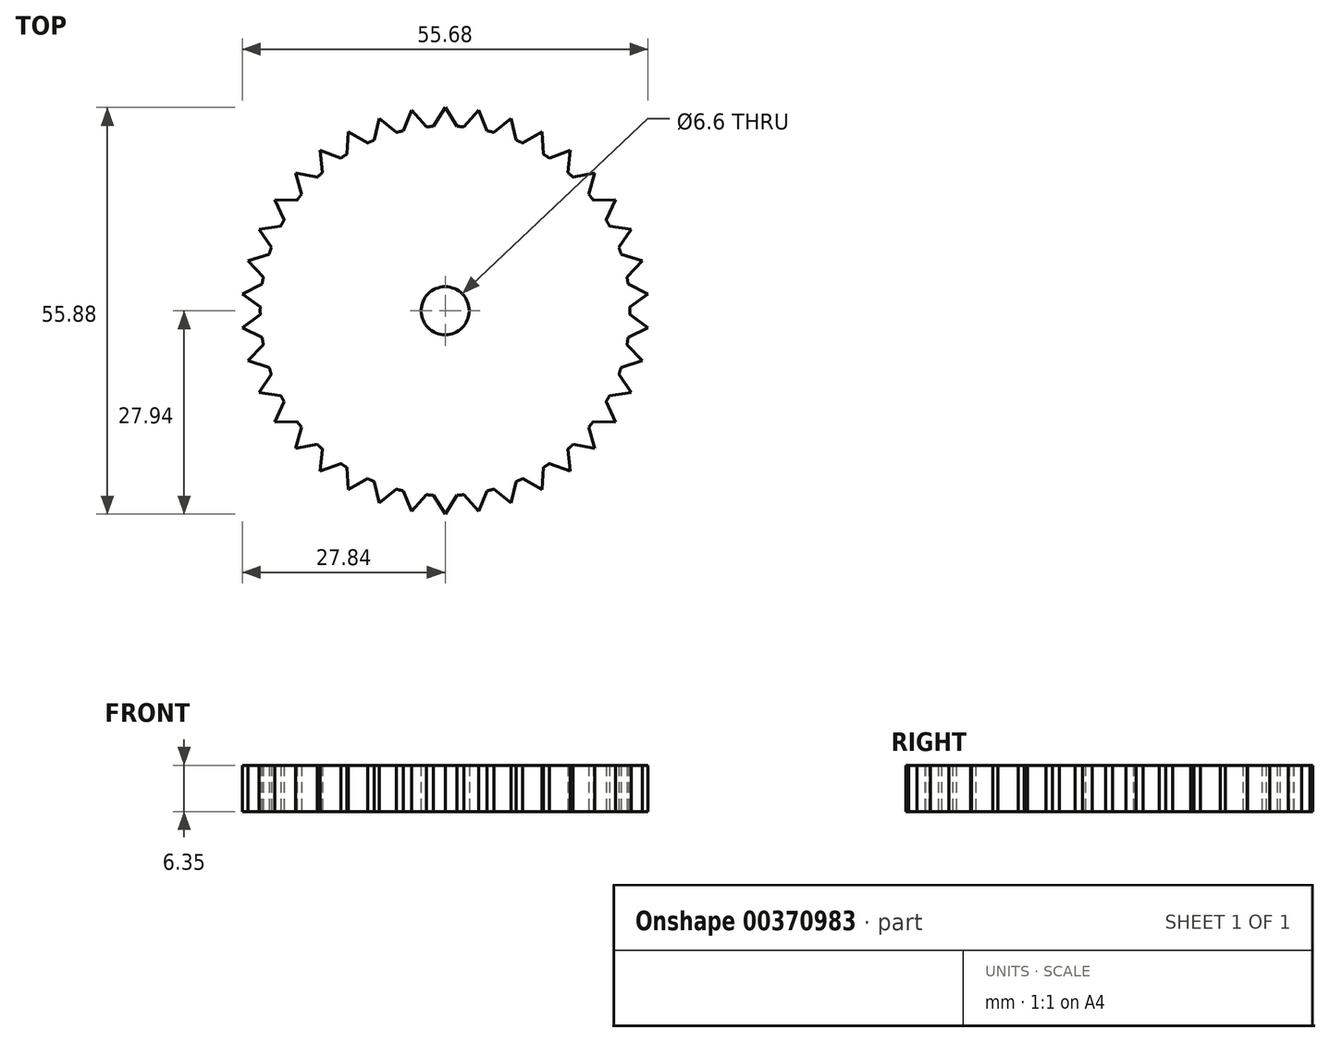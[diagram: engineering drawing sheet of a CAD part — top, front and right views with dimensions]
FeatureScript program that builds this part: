
annotation { "Feature Type Name" : "Feature", "Feature Type Description" : "" }
export const myFeature = defineFeature(function(context is Context, id is Id, definition is map)
    precondition{}
    {
        {
            var Q0;
            Q0=qCreatedBy(makeId("Top.planeOp"),FACE);
            var sketch = newSketch(context, id + "F0", { "sketchPlane" : qUnion([Q0])});
            skCircle(sketch, "E0", {"center": v(0, 0) * mm, "radius": 25.4 * mm});
            skCircle(sketch, "E1", {"center": v(0, 0) * mm, "radius": 3.3 * mm});
            skLineSegment(sketch, "E2", {"start": v(0, 25.4) * mm, "end": v(0, 27.94) * mm});
            skLineSegment(sketch, "E3", {"start": v(0, 27.94) * mm, "end": v(1.6, 25.35) * mm});
            skLineSegment(sketch, "E4", {"start": v(1.6, 25.35) * mm, "end": v(0, 27.94) * mm});
            skLineSegment(sketch, "E5", {"start": v(0, 27.94) * mm, "end": v(-1.6, 25.35) * mm});
            skLineSegment(sketch, "E6.1.0", {"start": v(-2.59, 25.27) * mm, "end": v(-4.6, 27.56) * mm});
            skLineSegment(sketch, "E6.1.1", {"start": v(-4.6, 27.56) * mm, "end": v(-5.76, 24.74) * mm});
            skLineSegment(sketch, "E6.2.0", {"start": v(-6.71, 24.5) * mm, "end": v(-9.07, 26.43) * mm});
            skLineSegment(sketch, "E6.2.1", {"start": v(-9.07, 26.43) * mm, "end": v(-9.75, 23.45) * mm});
            skLineSegment(sketch, "E6.3.0", {"start": v(-10.65, 23.06) * mm, "end": v(-13.3, 24.57) * mm});
            skLineSegment(sketch, "E6.3.1", {"start": v(-13.3, 24.57) * mm, "end": v(-13.48, 21.53) * mm});
            skLineSegment(sketch, "E6.4.0", {"start": v(-14.3, 21) * mm, "end": v(-17.16, 22.05) * mm});
            skLineSegment(sketch, "E6.4.1", {"start": v(-17.16, 22.05) * mm, "end": v(-16.84, 19.02) * mm});
            skLineSegment(sketch, "E6.5.0", {"start": v(-17.56, 18.35) * mm, "end": v(-20.56, 18.92) * mm});
            skLineSegment(sketch, "E6.5.1", {"start": v(-20.56, 18.92) * mm, "end": v(-19.74, 15.99) * mm});
            skLineSegment(sketch, "E6.6.0", {"start": v(-20.34, 15.2) * mm, "end": v(-23.4, 15.28) * mm});
            skLineSegment(sketch, "E6.6.1", {"start": v(-23.4, 15.28) * mm, "end": v(-22.1, 12.52) * mm});
            skLineSegment(sketch, "E6.7.0", {"start": v(-22.57, 11.65) * mm, "end": v(-25.59, 11.22) * mm});
            skLineSegment(sketch, "E6.7.1", {"start": v(-25.59, 11.22) * mm, "end": v(-23.86, 8.71) * mm});
            skLineSegment(sketch, "E6.8.0", {"start": v(-24.18, 7.78) * mm, "end": v(-27.09, 6.86) * mm});
            skLineSegment(sketch, "E6.8.1", {"start": v(-27.09, 6.86) * mm, "end": v(-24.97, 4.67) * mm});
            skLineSegment(sketch, "E6.9.0", {"start": v(-25.13, 3.7) * mm, "end": v(-27.84, 2.3) * mm});
            skLineSegment(sketch, "E6.9.1", {"start": v(-27.84, 2.3) * mm, "end": v(-25.4, 0.5) * mm});
            skLineSegment(sketch, "E6.10.0", {"start": v(-25.4, -0.5) * mm, "end": v(-27.84, -2.3) * mm});
            skLineSegment(sketch, "E6.10.1", {"start": v(-27.84, -2.3) * mm, "end": v(-25.13, -3.7) * mm});
            skLineSegment(sketch, "E6.11.0", {"start": v(-24.97, -4.67) * mm, "end": v(-27.09, -6.86) * mm});
            skLineSegment(sketch, "E6.11.1", {"start": v(-27.09, -6.86) * mm, "end": v(-24.18, -7.78) * mm});
            skLineSegment(sketch, "E6.12.0", {"start": v(-23.86, -8.71) * mm, "end": v(-25.59, -11.22) * mm});
            skLineSegment(sketch, "E6.12.1", {"start": v(-25.59, -11.22) * mm, "end": v(-22.57, -11.65) * mm});
            skLineSegment(sketch, "E6.13.0", {"start": v(-22.1, -12.52) * mm, "end": v(-23.4, -15.28) * mm});
            skLineSegment(sketch, "E6.13.1", {"start": v(-23.4, -15.28) * mm, "end": v(-20.34, -15.2) * mm});
            skLineSegment(sketch, "E6.14.0", {"start": v(-19.74, -15.99) * mm, "end": v(-20.56, -18.92) * mm});
            skLineSegment(sketch, "E6.14.1", {"start": v(-20.56, -18.92) * mm, "end": v(-17.56, -18.35) * mm});
            skLineSegment(sketch, "E6.15.0", {"start": v(-16.84, -19.02) * mm, "end": v(-17.16, -22.05) * mm});
            skLineSegment(sketch, "E6.15.1", {"start": v(-17.16, -22.05) * mm, "end": v(-14.3, -21) * mm});
            skLineSegment(sketch, "E6.16.0", {"start": v(-13.48, -21.53) * mm, "end": v(-13.3, -24.57) * mm});
            skLineSegment(sketch, "E6.16.1", {"start": v(-13.3, -24.57) * mm, "end": v(-10.65, -23.06) * mm});
            skLineSegment(sketch, "E6.17.0", {"start": v(-9.75, -23.45) * mm, "end": v(-9.07, -26.43) * mm});
            skLineSegment(sketch, "E6.17.1", {"start": v(-9.07, -26.43) * mm, "end": v(-6.71, -24.5) * mm});
            skLineSegment(sketch, "E6.18.0", {"start": v(-5.76, -24.74) * mm, "end": v(-4.6, -27.56) * mm});
            skLineSegment(sketch, "E6.18.1", {"start": v(-4.6, -27.56) * mm, "end": v(-2.59, -25.27) * mm});
            skLineSegment(sketch, "E6.19.0", {"start": v(-1.6, -25.35) * mm, "end": v(0, -27.94) * mm});
            skLineSegment(sketch, "E6.19.1", {"start": v(0, -27.94) * mm, "end": v(1.6, -25.35) * mm});
            skLineSegment(sketch, "E6.20.0", {"start": v(2.59, -25.27) * mm, "end": v(4.6, -27.56) * mm});
            skLineSegment(sketch, "E6.20.1", {"start": v(4.6, -27.56) * mm, "end": v(5.76, -24.74) * mm});
            skLineSegment(sketch, "E6.21.0", {"start": v(6.71, -24.5) * mm, "end": v(9.07, -26.43) * mm});
            skLineSegment(sketch, "E6.21.1", {"start": v(9.07, -26.43) * mm, "end": v(9.75, -23.45) * mm});
            skLineSegment(sketch, "E6.22.0", {"start": v(10.65, -23.06) * mm, "end": v(13.3, -24.57) * mm});
            skLineSegment(sketch, "E6.22.1", {"start": v(13.3, -24.57) * mm, "end": v(13.48, -21.53) * mm});
            skLineSegment(sketch, "E6.23.0", {"start": v(14.3, -21) * mm, "end": v(17.16, -22.05) * mm});
            skLineSegment(sketch, "E6.23.1", {"start": v(17.16, -22.05) * mm, "end": v(16.84, -19.02) * mm});
            skLineSegment(sketch, "E6.24.0", {"start": v(17.56, -18.35) * mm, "end": v(20.56, -18.92) * mm});
            skLineSegment(sketch, "E6.24.1", {"start": v(20.56, -18.92) * mm, "end": v(19.74, -15.99) * mm});
            skLineSegment(sketch, "E6.25.0", {"start": v(20.34, -15.2) * mm, "end": v(23.4, -15.28) * mm});
            skLineSegment(sketch, "E6.25.1", {"start": v(23.4, -15.28) * mm, "end": v(22.1, -12.52) * mm});
            skLineSegment(sketch, "E6.26.0", {"start": v(22.57, -11.65) * mm, "end": v(25.59, -11.22) * mm});
            skLineSegment(sketch, "E6.26.1", {"start": v(25.59, -11.22) * mm, "end": v(23.86, -8.71) * mm});
            skLineSegment(sketch, "E6.27.0", {"start": v(24.18, -7.78) * mm, "end": v(27.09, -6.86) * mm});
            skLineSegment(sketch, "E6.27.1", {"start": v(27.09, -6.86) * mm, "end": v(24.97, -4.67) * mm});
            skLineSegment(sketch, "E6.28.0", {"start": v(25.13, -3.7) * mm, "end": v(27.84, -2.3) * mm});
            skLineSegment(sketch, "E6.28.1", {"start": v(27.84, -2.3) * mm, "end": v(25.4, -0.5) * mm});
            skLineSegment(sketch, "E6.29.0", {"start": v(25.4, 0.5) * mm, "end": v(27.84, 2.3) * mm});
            skLineSegment(sketch, "E6.29.1", {"start": v(27.84, 2.3) * mm, "end": v(25.13, 3.7) * mm});
            skLineSegment(sketch, "E6.30.0", {"start": v(24.97, 4.67) * mm, "end": v(27.09, 6.86) * mm});
            skLineSegment(sketch, "E6.30.1", {"start": v(27.09, 6.86) * mm, "end": v(24.18, 7.78) * mm});
            skLineSegment(sketch, "E6.31.0", {"start": v(23.86, 8.71) * mm, "end": v(25.59, 11.22) * mm});
            skLineSegment(sketch, "E6.31.1", {"start": v(25.59, 11.22) * mm, "end": v(22.57, 11.65) * mm});
            skLineSegment(sketch, "E6.32.0", {"start": v(22.1, 12.52) * mm, "end": v(23.4, 15.28) * mm});
            skLineSegment(sketch, "E6.32.1", {"start": v(23.4, 15.28) * mm, "end": v(20.34, 15.2) * mm});
            skLineSegment(sketch, "E6.33.0", {"start": v(19.74, 15.99) * mm, "end": v(20.56, 18.92) * mm});
            skLineSegment(sketch, "E6.33.1", {"start": v(20.56, 18.92) * mm, "end": v(17.56, 18.35) * mm});
            skLineSegment(sketch, "E6.34.0", {"start": v(16.84, 19.02) * mm, "end": v(17.16, 22.05) * mm});
            skLineSegment(sketch, "E6.34.1", {"start": v(17.16, 22.05) * mm, "end": v(14.3, 21) * mm});
            skLineSegment(sketch, "E6.35.0", {"start": v(13.48, 21.53) * mm, "end": v(13.3, 24.57) * mm});
            skLineSegment(sketch, "E6.35.1", {"start": v(13.3, 24.57) * mm, "end": v(10.65, 23.06) * mm});
            skLineSegment(sketch, "E6.36.0", {"start": v(9.75, 23.45) * mm, "end": v(9.07, 26.43) * mm});
            skLineSegment(sketch, "E6.36.1", {"start": v(9.07, 26.43) * mm, "end": v(6.71, 24.5) * mm});
            skLineSegment(sketch, "E6.37.0", {"start": v(5.76, 24.74) * mm, "end": v(4.6, 27.56) * mm});
            skLineSegment(sketch, "E6.37.1", {"start": v(4.6, 27.56) * mm, "end": v(2.59, 25.27) * mm});
            skSolve(sketch);
        }
        {
            var Q0;
            {var subQ0=sQuery(id+"F0.wireOp",EDGE,"E6.37.0");Q0=makeQuery(id+"F0.imprint","IMPRINT",FACE,{"disambiguationData":[TD([[makeQuery(id+"F0.imprint","IMPRINT",EDGE,{"derivedFrom":subQ0}),1.0]])]});}
            var Q1;
            {var subQ0=sQuery(id+"F0.wireOp",EDGE,"E6.36.0");Q1=makeQuery(id+"F0.imprint","IMPRINT",FACE,{"disambiguationData":[TD([[makeQuery(id+"F0.imprint","IMPRINT",EDGE,{"derivedFrom":subQ0}),1.0]])]});}
            var Q2;
            {var subQ0=sQuery(id+"F0.wireOp",EDGE,"E6.35.0");Q2=makeQuery(id+"F0.imprint","IMPRINT",FACE,{"disambiguationData":[TD([[makeQuery(id+"F0.imprint","IMPRINT",EDGE,{"derivedFrom":subQ0}),1.0]])]});}
            var Q3;
            {var subQ0=sQuery(id+"F0.wireOp",EDGE,"E6.34.0");Q3=makeQuery(id+"F0.imprint","IMPRINT",FACE,{"disambiguationData":[TD([[makeQuery(id+"F0.imprint","IMPRINT",EDGE,{"derivedFrom":subQ0}),1.0]])]});}
            var Q4;
            {var subQ0=sQuery(id+"F0.wireOp",EDGE,"E6.33.0");Q4=makeQuery(id+"F0.imprint","IMPRINT",FACE,{"disambiguationData":[TD([[makeQuery(id+"F0.imprint","IMPRINT",EDGE,{"derivedFrom":subQ0}),1.0]])]});}
            var Q5;
            {var subQ0=sQuery(id+"F0.wireOp",EDGE,"E6.32.0");Q5=makeQuery(id+"F0.imprint","IMPRINT",FACE,{"disambiguationData":[TD([[makeQuery(id+"F0.imprint","IMPRINT",EDGE,{"derivedFrom":subQ0}),1.0]])]});}
            var Q6;
            {var subQ0=sQuery(id+"F0.wireOp",EDGE,"E6.31.0");Q6=makeQuery(id+"F0.imprint","IMPRINT",FACE,{"disambiguationData":[TD([[makeQuery(id+"F0.imprint","IMPRINT",EDGE,{"derivedFrom":subQ0}),1.0]])]});}
            var Q7;
            {var subQ0=sQuery(id+"F0.wireOp",EDGE,"E6.30.0");Q7=makeQuery(id+"F0.imprint","IMPRINT",FACE,{"disambiguationData":[TD([[makeQuery(id+"F0.imprint","IMPRINT",EDGE,{"derivedFrom":subQ0}),1.0]])]});}
            var Q8;
            {var subQ0=sQuery(id+"F0.wireOp",EDGE,"E6.29.0");Q8=makeQuery(id+"F0.imprint","IMPRINT",FACE,{"disambiguationData":[TD([[makeQuery(id+"F0.imprint","IMPRINT",EDGE,{"derivedFrom":subQ0}),1.0]])]});}
            var Q9;
            {var subQ0=sQuery(id+"F0.wireOp",EDGE,"E6.28.0");Q9=makeQuery(id+"F0.imprint","IMPRINT",FACE,{"disambiguationData":[TD([[makeQuery(id+"F0.imprint","IMPRINT",EDGE,{"derivedFrom":subQ0}),1.0]])]});}
            var Q10;
            {var subQ0=sQuery(id+"F0.wireOp",EDGE,"E6.27.0");Q10=makeQuery(id+"F0.imprint","IMPRINT",FACE,{"disambiguationData":[TD([[makeQuery(id+"F0.imprint","IMPRINT",EDGE,{"derivedFrom":subQ0}),1.0]])]});}
            var Q11;
            {var subQ0=sQuery(id+"F0.wireOp",EDGE,"E6.26.0");Q11=makeQuery(id+"F0.imprint","IMPRINT",FACE,{"disambiguationData":[TD([[makeQuery(id+"F0.imprint","IMPRINT",EDGE,{"derivedFrom":subQ0}),1.0]])]});}
            var Q12;
            {var subQ0=sQuery(id+"F0.wireOp",EDGE,"E6.25.0");Q12=makeQuery(id+"F0.imprint","IMPRINT",FACE,{"disambiguationData":[TD([[makeQuery(id+"F0.imprint","IMPRINT",EDGE,{"derivedFrom":subQ0}),1.0]])]});}
            var Q13;
            {var subQ0=sQuery(id+"F0.wireOp",EDGE,"E6.24.0");Q13=makeQuery(id+"F0.imprint","IMPRINT",FACE,{"disambiguationData":[TD([[makeQuery(id+"F0.imprint","IMPRINT",EDGE,{"derivedFrom":subQ0}),1.0]])]});}
            var Q14;
            {var subQ0=sQuery(id+"F0.wireOp",EDGE,"E6.23.0");Q14=makeQuery(id+"F0.imprint","IMPRINT",FACE,{"disambiguationData":[TD([[makeQuery(id+"F0.imprint","IMPRINT",EDGE,{"derivedFrom":subQ0}),1.0]])]});}
            var Q15;
            {var subQ0=sQuery(id+"F0.wireOp",EDGE,"E6.22.0");Q15=makeQuery(id+"F0.imprint","IMPRINT",FACE,{"disambiguationData":[TD([[makeQuery(id+"F0.imprint","IMPRINT",EDGE,{"derivedFrom":subQ0}),1.0]])]});}
            var Q16;
            {var subQ0=sQuery(id+"F0.wireOp",EDGE,"E6.21.0");Q16=makeQuery(id+"F0.imprint","IMPRINT",FACE,{"disambiguationData":[TD([[makeQuery(id+"F0.imprint","IMPRINT",EDGE,{"derivedFrom":subQ0}),1.0]])]});}
            var Q17;
            {var subQ0=sQuery(id+"F0.wireOp",EDGE,"E6.11.0");Q17=makeQuery(id+"F0.imprint","IMPRINT",FACE,{"disambiguationData":[TD([[makeQuery(id+"F0.imprint","IMPRINT",EDGE,{"derivedFrom":subQ0}),1.0]])]});}
            var Q18;
            {var subQ0=sQuery(id+"F0.wireOp",EDGE,"E6.12.0");Q18=makeQuery(id+"F0.imprint","IMPRINT",FACE,{"disambiguationData":[TD([[makeQuery(id+"F0.imprint","IMPRINT",EDGE,{"derivedFrom":subQ0}),1.0]])]});}
            var Q19;
            {var subQ0=sQuery(id+"F0.wireOp",EDGE,"E6.13.0");Q19=makeQuery(id+"F0.imprint","IMPRINT",FACE,{"disambiguationData":[TD([[makeQuery(id+"F0.imprint","IMPRINT",EDGE,{"derivedFrom":subQ0}),1.0]])]});}
            var Q20;
            {var subQ0=sQuery(id+"F0.wireOp",EDGE,"E6.14.0");Q20=makeQuery(id+"F0.imprint","IMPRINT",FACE,{"disambiguationData":[TD([[makeQuery(id+"F0.imprint","IMPRINT",EDGE,{"derivedFrom":subQ0}),1.0]])]});}
            var Q21;
            {var subQ0=sQuery(id+"F0.wireOp",EDGE,"E6.7.0");Q21=makeQuery(id+"F0.imprint","IMPRINT",FACE,{"disambiguationData":[TD([[makeQuery(id+"F0.imprint","IMPRINT",EDGE,{"derivedFrom":subQ0}),1.0]])]});}
            var Q22;
            {var subQ0=sQuery(id+"F0.wireOp",EDGE,"E6.8.0");Q22=makeQuery(id+"F0.imprint","IMPRINT",FACE,{"disambiguationData":[TD([[makeQuery(id+"F0.imprint","IMPRINT",EDGE,{"derivedFrom":subQ0}),1.0]])]});}
            var Q23;
            {var subQ0=sQuery(id+"F0.wireOp",EDGE,"E6.6.0");Q23=makeQuery(id+"F0.imprint","IMPRINT",FACE,{"disambiguationData":[TD([[makeQuery(id+"F0.imprint","IMPRINT",EDGE,{"derivedFrom":subQ0}),1.0]])]});}
            var Q24;
            {var subQ0=sQuery(id+"F0.wireOp",EDGE,"E6.2.0");Q24=makeQuery(id+"F0.imprint","IMPRINT",FACE,{"disambiguationData":[TD([[makeQuery(id+"F0.imprint","IMPRINT",EDGE,{"derivedFrom":subQ0}),1.0]])]});}
            var Q25;
            {var subQ0=sQuery(id+"F0.wireOp",EDGE,"E6.4.0");Q25=makeQuery(id+"F0.imprint","IMPRINT",FACE,{"disambiguationData":[TD([[makeQuery(id+"F0.imprint","IMPRINT",EDGE,{"derivedFrom":subQ0}),1.0]])]});}
            var Q26;
            {var subQ0=sQuery(id+"F0.wireOp",EDGE,"E6.15.0");Q26=makeQuery(id+"F0.imprint","IMPRINT",FACE,{"disambiguationData":[TD([[makeQuery(id+"F0.imprint","IMPRINT",EDGE,{"derivedFrom":subQ0}),1.0]])]});}
            var Q27;
            {var subQ0=sQuery(id+"F0.wireOp",EDGE,"E6.9.0");Q27=makeQuery(id+"F0.imprint","IMPRINT",FACE,{"disambiguationData":[TD([[makeQuery(id+"F0.imprint","IMPRINT",EDGE,{"derivedFrom":subQ0}),1.0]])]});}
            var Q28;
            {var subQ0=sQuery(id+"F0.wireOp",EDGE,"E6.16.0");Q28=makeQuery(id+"F0.imprint","IMPRINT",FACE,{"disambiguationData":[TD([[makeQuery(id+"F0.imprint","IMPRINT",EDGE,{"derivedFrom":subQ0}),1.0]])]});}
            var Q29;
            {var subQ0=sQuery(id+"F0.wireOp",EDGE,"E6.10.0");Q29=makeQuery(id+"F0.imprint","IMPRINT",FACE,{"disambiguationData":[TD([[makeQuery(id+"F0.imprint","IMPRINT",EDGE,{"derivedFrom":subQ0}),1.0]])]});}
            var Q30;
            {var subQ0=sQuery(id+"F0.wireOp",EDGE,"E6.18.0");Q30=makeQuery(id+"F0.imprint","IMPRINT",FACE,{"disambiguationData":[TD([[makeQuery(id+"F0.imprint","IMPRINT",EDGE,{"derivedFrom":subQ0}),1.0]])]});}
            var Q31;
            {var subQ0=sQuery(id+"F0.wireOp",EDGE,"E6.19.0");Q31=makeQuery(id+"F0.imprint","IMPRINT",FACE,{"disambiguationData":[TD([[makeQuery(id+"F0.imprint","IMPRINT",EDGE,{"derivedFrom":subQ0}),1.0]])]});}
            var Q32;
            {var subQ0=sQuery(id+"F0.wireOp",EDGE,"E6.20.0");Q32=makeQuery(id+"F0.imprint","IMPRINT",FACE,{"disambiguationData":[TD([[makeQuery(id+"F0.imprint","IMPRINT",EDGE,{"derivedFrom":subQ0}),1.0]])]});}
            var Q33;
            {var subQ0=sQuery(id+"F0.wireOp",EDGE,"E6.5.0");Q33=makeQuery(id+"F0.imprint","IMPRINT",FACE,{"disambiguationData":[TD([[makeQuery(id+"F0.imprint","IMPRINT",EDGE,{"derivedFrom":subQ0}),1.0]])]});}
            var Q34;
            {var subQ0=sQuery(id+"F0.wireOp",EDGE,"E6.1.0");Q34=makeQuery(id+"F0.imprint","IMPRINT",FACE,{"disambiguationData":[TD([[makeQuery(id+"F0.imprint","IMPRINT",EDGE,{"derivedFrom":subQ0}),1.0]])]});}
            var Q35;
            {var subQ0=sQuery(id+"F0.wireOp",EDGE,"E6.3.0");Q35=makeQuery(id+"F0.imprint","IMPRINT",FACE,{"disambiguationData":[TD([[makeQuery(id+"F0.imprint","IMPRINT",EDGE,{"derivedFrom":subQ0}),1.0]])]});}
            var Q36;
            {var subQ0=sQuery(id+"F0.wireOp",EDGE,"E6.17.0");Q36=makeQuery(id+"F0.imprint","IMPRINT",FACE,{"disambiguationData":[TD([[makeQuery(id+"F0.imprint","IMPRINT",EDGE,{"derivedFrom":subQ0}),1.0]])]});}
            var Q37;
            {var subQ0=sQuery(id+"F0.wireOp",EDGE,"E2");Q37=makeQuery(id+"F0.imprint","IMPRINT",FACE,{"disambiguationData":[TD([[makeQuery(id+"F0.imprint","IMPRINT",EDGE,{"derivedFrom":subQ0}),-1.0]])]});}
            var Q38;
            {var subQ0=sQuery(id+"F0.wireOp",EDGE,"E2");Q38=makeQuery(id+"F0.imprint","IMPRINT",FACE,{"disambiguationData":[TD([[makeQuery(id+"F0.imprint","IMPRINT",EDGE,{"derivedFrom":subQ0}),1.0]])]});}
            var Q39;
            Q39=makeQuery(id+"F0.imprint","IMPRINT",FACE,{"disambiguationData":[TD([[makeQuery(id+"F0.imprint","IMPRINT",EDGE,{"derivedFrom":sQuery(id+"F0.wireOp",EDGE,"E1")}),-1.0]])]});
            extrude(context, id + "F1", {"entities" : qUnion([Q0, Q1, Q2, Q3, Q4, Q5, Q6, Q7, Q8, Q9, Q10, Q11, Q12, Q13, Q14, Q15, Q16, Q17, Q18, Q19, Q20, Q21, Q22, Q23, Q24, Q25, Q26, Q27, Q28, Q29, Q30, Q31, Q32, Q33, Q34, Q35, Q36, Q37, Q38, Q39]), "depth" : 6.35 * mm});
        }
    });
